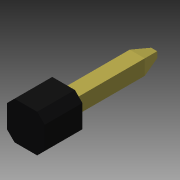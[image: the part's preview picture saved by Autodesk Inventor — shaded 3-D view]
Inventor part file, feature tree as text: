
AUTODESK INVENTOR PART (.ipt)
format: ipt  version: 2013 SP2 (Build 170200200, 200)  size: 109,056 bytes
history: native  units: mm
features: extrude x2, chamfer x2, sketch x2
ambient origin geometry x8: Origin, YZ Plane, XZ Plane, XY Plane, X Axis, Y Axis, Z Axis, Center Point
bodies: Solid1 (feature_tree)
feature tree (6):
  extrude  "Extrusion1"  Depth=2.5mm
  chamfer  "Chamfer1"  Distance=2.5mm
  extrude  "Extrusion2"  Depth=1.0mm
  chamfer  "Chamfer2"  Distance=1.0mm
  sketch  "Sketch1"  dims[d0=2.5mm d1=2.5mm d2=2.5mm d3=0.0mm]
  sketch  "Sketch2"  dims[d4=0.5mm d5=2.0mm d6=45.0deg d7=1.0mm d9=1.0mm d10=0.5mm d11=0.5mm d12=6.0mm d13=0.0mm d14=0.3mm d15=2.0mm d16=75.0deg]
